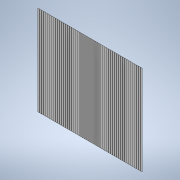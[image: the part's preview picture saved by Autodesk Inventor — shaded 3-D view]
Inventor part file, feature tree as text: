
AUTODESK INVENTOR PART (.ipt)
format: ipt  version: 2021 (Build 250183000, 183)  size: 296,448 bytes
history: native  units: in
note: dims shown in document units (in); Inventor stores cm internally (conversion verified against a paired STEP export)
features: extrude x3, sketch x3, pattern_linear x1, projected_geometry x1
ambient origin geometry x8: Origin, YZ Plane, XZ Plane, XY Plane, X Axis, Y Axis, Z Axis, Center Point
bodies: Solid1 (feature_tree)
feature tree (8):
  extrude  "Extrusion1"  Depth=3.0in
  extrude  "Extrusion2"  Depth=0.06in
  pattern_linear  "Rectangular Pattern1"  Count1=53 Spacing1=0.066in
  extrude  "Extrusion3"  Depth=0.066in TaperAngle=0.0deg
  sketch  "Sketch1"  dims[d0=4.0in d1=3.0in]
  sketch  "Sketch2"  dims[d2=0.04in d3=0.0in d4=0.06in]
  projected_geometry  "Projected Loop1"
  sketch  "Sketch3"  dims[d5=0.0015in d6=0.0in d7=20.8661in d9=0.066in d10=1.0in d11=0.0in]
